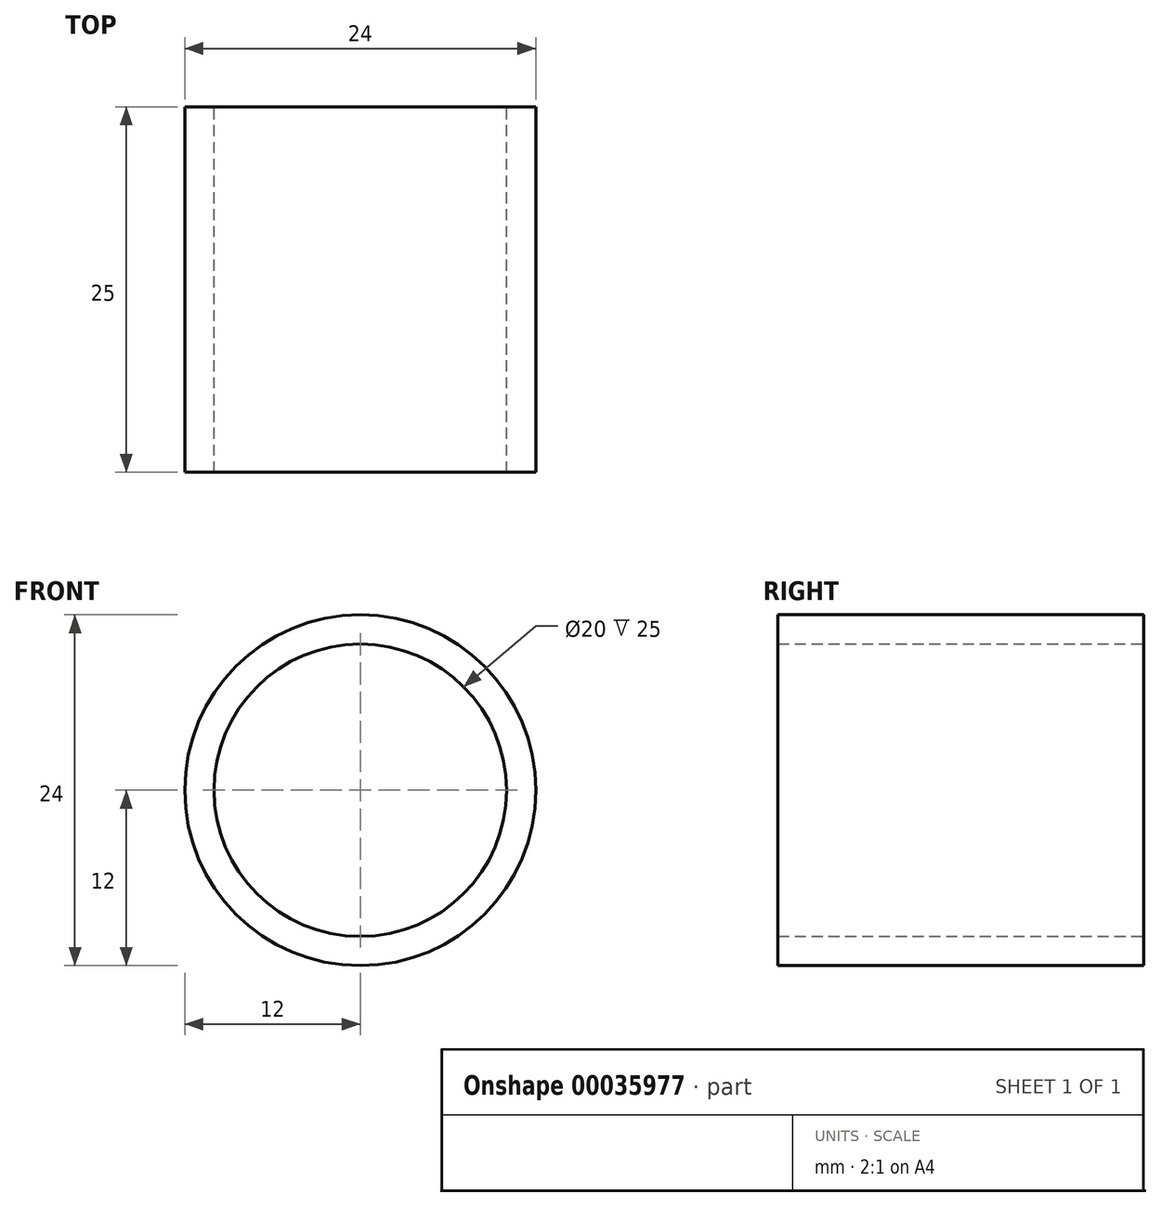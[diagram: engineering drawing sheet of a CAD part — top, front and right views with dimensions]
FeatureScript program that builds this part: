
annotation { "Feature Type Name" : "Feature", "Feature Type Description" : "" }
export const myFeature = defineFeature(function(context is Context, id is Id, definition is map)
    precondition{}
    {
        {
            var Q0;
            Q0=qCreatedBy(makeId("Front.planeOp"),FACE);
            var sketch = newSketch(context, id + "F0", { "sketchPlane" : qUnion([Q0])});
            skCircle(sketch, "E0", {"center": v(0, 0) * mm, "radius": 10 * mm});
            skCircle(sketch, "E1", {"center": v(0, 0) * mm, "radius": 12 * mm});
            skSolve(sketch);
        }
        {
            var Q0;
            Q0=makeQuery(id+"F0.imprint","IMPRINT",FACE,{"disambiguationData":[TD([[makeQuery(id+"F0.imprint","IMPRINT",EDGE,{"derivedFrom":sQuery(id+"F0.wireOp",EDGE,"E0")}),-1.0]])]});
            extrude(context, id + "F1", {"entities" : qUnion([Q0]), "depth" : 25 * mm});
        }
    });
